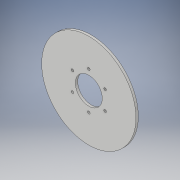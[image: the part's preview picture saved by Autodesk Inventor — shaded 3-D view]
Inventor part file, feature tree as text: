
AUTODESK INVENTOR PART (.ipt)
format: ipt  version: 2019 (Build 230136000, 136)  size: 115,712 bytes
history: native  units: in
note: dims shown in document units (in); Inventor stores cm internally (conversion verified against a paired STEP export)
features: extrude x2, sketch x2
ambient origin geometry x8: Origin, YZ Plane, XZ Plane, XY Plane, X Axis, Y Axis, Z Axis, Center Point
bodies: Solid1 (feature_tree)
feature tree (4):
  extrude  "Extrusion1"  Depth=10.0in
  extrude  "Extrusion3"  Depth=0.25in
  sketch  "Sketch1"  dims[d0=2.85in d1=10.0in]
  sketch  "Sketch3"  dims[d2=0.25in d3=0.0in d13=4.0in d14=0.266in d15=2.3622in d17=360.0deg d19=0.25in d20=0.0in]
